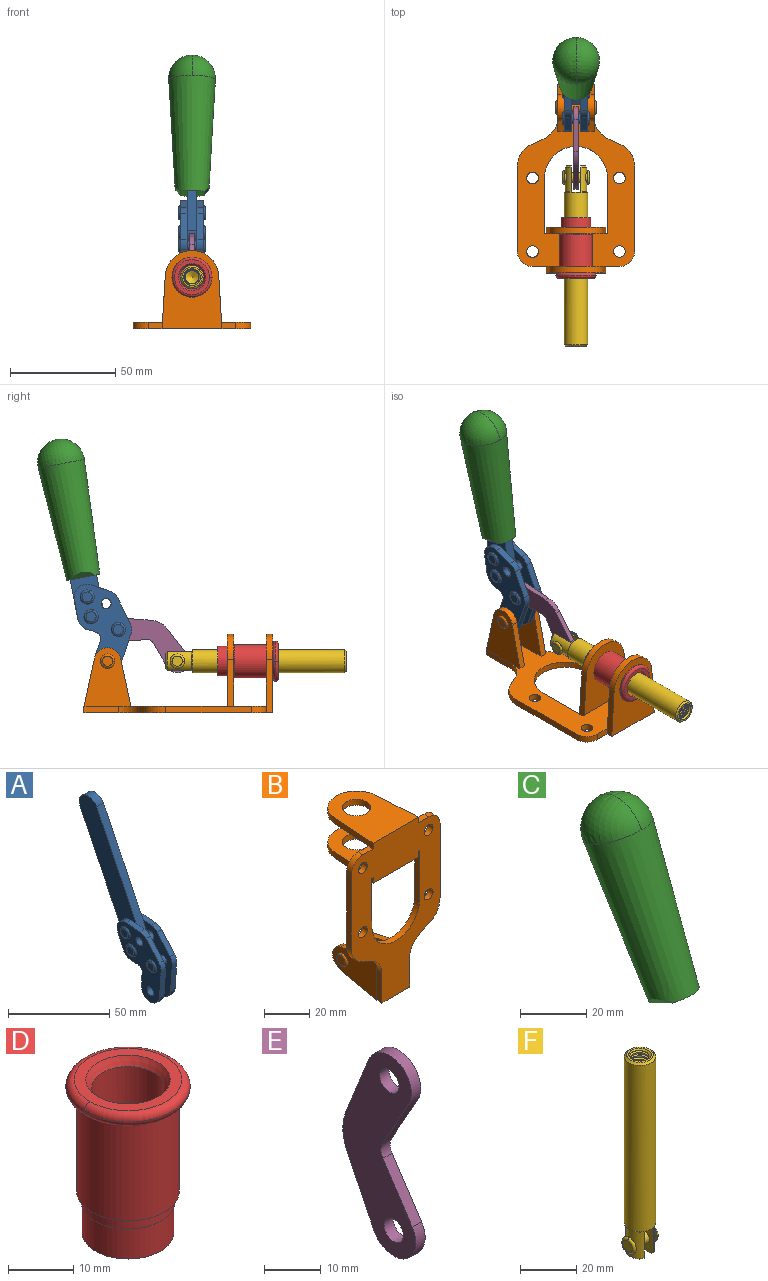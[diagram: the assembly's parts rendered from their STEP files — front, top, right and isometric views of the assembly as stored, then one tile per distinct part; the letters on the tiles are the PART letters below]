
ASSEMBLY  parts=6 mates=6
PART A: 59 faces, bbox 12.9x60.2x99.6 mm
  f0: torus R=2.39mm, axis (-1,0,0), area 14.9mm2, adj f20,f43,f51
  f1: torus R=2.39mm, axis (-1,0,0), area 14.9mm2, adj f19,f42,f51
  f2: torus R=2.39mm, axis (-1,0,0), area 14.9mm2, adj f18,f35,f51
  f3: torus R=2.39mm, axis (-1,0,0), area 14.9mm2, adj f14,f17,f23
  f4: torus R=2.39mm, axis (-1,0,0), area 14.9mm2, adj f13,f16,f23
  f5: torus R=2.39mm, axis (-1,0,0), area 14.9mm2, adj f12,f15,f23
  f6: cylinder r=2.39mm len=4.78mm, axis (1,0,0), area 46.5mm2, adj f48,f50,f51
  f7: cylinder r=2.39mm len=4.78mm, axis (1,0,0), area 46.5mm2, adj f50,f51
  f8: cylinder r=6.35mm len=12.68mm, axis (1,0,0), area 61.8mm2, adj f38,f39,f50,f51
  f9: cylinder r=2.39mm len=4.78mm, axis (-1,0,0), area 70.5mm2, adj f46,f50
  f10: cylinder r=2.39mm len=4.78mm, axis (-1,0,0), area 46.5mm2, adj f23,f45,f46
  f11: cylinder r=2.39mm len=4.78mm, axis (-1,0,0), area 46.5mm2, adj f23,f46
  f12: plane 4.78x4.78mm, normal (1,0,0), area 17.9mm2, adj f5,f15
  f13: plane 4.78x4.78mm, normal (1,0,0), area 17.9mm2, adj f4,f16
  f14: plane 4.78x4.78mm, normal (1,0,0), area 17.9mm2, adj f3,f17
  f15: torus R=2.39mm, axis (-1,0,0), area 14.9mm2, adj f5,f12,f23
  f16: torus R=2.39mm, axis (-1,0,0), area 14.9mm2, adj f4,f13,f23
  f17: torus R=2.39mm, axis (-1,0,0), area 14.9mm2, adj f3,f14,f23
  f18: plane 4.78x4.78mm, normal (-1,0,0), area 17.9mm2, adj f2,f35
  f19: plane 4.78x4.78mm, normal (-1,0,0), area 17.9mm2, adj f1,f42
  f20: plane 4.78x4.78mm, normal (-1,0,0), area 17.9mm2, adj f0,f43
  f21: plane 2.26x0.2mm, normal (1,0,0), area 0.2mm2, adj f31,f44
  f22: plane 2.26x0.2mm, normal (-1,0,0), area 0.2mm2, adj f41,f44
  f23: plane 39.37x30.77mm, normal (1,0,0), area 565.5mm2, adj f3,f4,f5,f10,f11,f15,f16,f17
  f24: cylinder r=6.1mm len=4.15mm, axis (-1,0,0), area 14.7mm2, adj f23,f25,f32,f46
  f25: plane 10.25x9.01mm, normal (0,-0.75,0.66), area 42.3mm2, adj f23,f24,f26,f46
  f26: cylinder r=6.35mm len=4.64mm, axis (-1,0,0), area 15.6mm2, adj f23,f25,f27,f46
  f27: plane 15.84x3.1mm, normal (0,-1,-0.07), area 49.2mm2, adj f23,f26,f28,f46
  f28: cylinder r=6.35mm len=12.68mm, axis (-1,0,0), area 61.8mm2, adj f23,f27,f29,f46
  f29: plane 8.11x3.1mm, normal (0,1,0.07), area 25.2mm2, adj f23,f28,f30,f46
  f30: cylinder r=3.05mm len=3.25mm, axis (-1,0,0), area 14.8mm2, adj f23,f29,f31,f46
  f31: plane 5.99x3.1mm, normal (0,0.07,-1), area 18.6mm2, adj f21,f23,f30,f44,f46
  f32: plane 9.5x3.1mm, normal (0,-0.07,1), area 29.5mm2, adj f23,f24,f33,f46,f47
  f33: cylinder r=6.1mm len=8.63mm, axis (-1,0,0), area 39.1mm2, adj f23,f32,f34,f47
  f34: plane 8.65x3.96mm, normal (0,0.91,-0.42), area 29.5mm2, adj f23,f33,f44,f47
  f35: torus R=2.39mm, axis (-1,0,0), area 14.9mm2, adj f2,f18,f51
  f36: plane 10.25x9.01mm, normal (0,-0.75,0.66), area 42.3mm2, adj f37,f49,f50,f51
  f37: cylinder r=6.35mm len=4.64mm, axis (1,0,0), area 15.6mm2, adj f36,f38,f50,f51
  f38: plane 15.84x3.1mm, normal (0,-1,-0.07), area 49.2mm2, adj f8,f37,f50,f51
  f39: plane 8.11x3.1mm, normal (0,1,0.07), area 25.2mm2, adj f8,f40,f50,f51
  f40: cylinder r=3.05mm len=3.25mm, axis (1,0,0), area 14.8mm2, adj f39,f41,f50,f51
  f41: plane 5.99x3.1mm, normal (0,0.07,-1), area 18.6mm2, adj f22,f40,f44,f50,f51
  f42: torus R=2.39mm, axis (-1,0,0), area 14.9mm2, adj f1,f19,f51
  f43: torus R=2.39mm, axis (-1,0,0), area 14.9mm2, adj f0,f20,f51
  f44: cylinder r=6.35mm len=12.12mm, axis (-1,0,0), area 128.9mm2, adj f21,f22,f23,f31,f34,f41,f46,f47
  f45: plane 2.65x1.35mm, normal (1,0,0), area 1mm2, adj f10,f55
  f46: plane 39.08x20.42mm, normal (-1,0,0), area 412.5mm2, adj f9,f10,f11,f24,f25,f26,f27,f28
  f47: plane 77.62x39.82mm, normal (1,0,0), area 850mm2, adj f32,f33,f34,f44,f53,f54,f55
  f48: plane 2.65x1.35mm, normal (-1,0,0), area 1mm2, adj f6,f55
  f49: cylinder r=6.1mm len=4.15mm, axis (1,0,0), area 14.7mm2, adj f36,f50,f51,f56
  f50: plane 39.08x20.42mm, normal (1,0,0), area 412.5mm2, adj f6,f7,f8,f9,f36,f37,f38,f39
  f51: plane 39.37x30.77mm, normal (-1,0,0), area 565.5mm2, adj f0,f1,f2,f6,f7,f8,f35,f36
  f52: plane 8.65x3.96mm, normal (0,0.91,-0.42), area 29.5mm2, adj f44,f51,f57,f58
  f53: plane 68.49x33.4mm, normal (0,0.9,-0.44), area 358.1mm2, adj f44,f47,f54,f58
  f54: cylinder r=6.35mm len=12.06mm, axis (1,0,0), area 93.7mm2, adj f47,f53,f55,f58
  f55: plane 68.49x33.4mm, normal (0,-0.9,0.44), area 358.1mm2, adj f44,f45,f46,f47,f48,f50,f54,f58
  f56: plane 9.5x3.1mm, normal (0,-0.07,1), area 29.5mm2, adj f49,f50,f51,f57,f58
  f57: cylinder r=6.1mm len=8.63mm, axis (1,0,0), area 39.1mm2, adj f51,f52,f56,f58
  f58: plane 77.62x39.82mm, normal (-1,0,0), area 850mm2, adj f44,f52,f53,f54,f55,f56,f57
PART B: 55 faces, bbox 55.7x37.4x89.8 mm
  f0: torus R=2.41mm, axis (-1,0,0), area 15mm2, adj f11,f15,f25
  f1: torus R=2.41mm, axis (-1,0,0), area 15mm2, adj f10,f12,f22
  f2: cylinder r=2.78mm len=5.56mm, axis (0,-1,0), area 54.2mm2, adj f30,f54
  f3: cylinder r=14.99mm len=29.97mm, axis (0,-1,0), area 145.9mm2, adj f30,f49,f53,f54
  f4: cylinder r=2.78mm len=5.56mm, axis (0,-1,0), area 54.2mm2, adj f30,f54
  f5: cylinder r=2.78mm len=5.56mm, axis (0,-1,0), area 54.2mm2, adj f30,f54
  f6: cylinder r=2.78mm len=5.56mm, axis (0,-1,0), area 54.2mm2, adj f30,f54
  f7: cylinder r=6.35mm len=12.7mm, axis (0,0,1), area 123.6mm2, adj f27,f51
  f8: cylinder r=6.35mm len=12.7mm, axis (0,0,-1), area 124.7mm2, adj f21,f35
  f9: cylinder r=2.41mm len=11.18mm, axis (-1,0,0), area 169.4mm2, adj f16,f19
  f10: plane 4.83x4.83mm, normal (1,0,0), area 18.3mm2, adj f1,f12
  f11: plane 4.83x4.83mm, normal (-1,0,0), area 18.3mm2, adj f0,f15
  f12: torus R=2.41mm, axis (-1,0,0), area 15mm2, adj f1,f10,f22
  f13: cylinder r=6.35mm len=12.41mm, axis (1,0,0), area 53.4mm2, adj f18,f19,f22,f23
  f14: cylinder r=6.35mm len=12.41mm, axis (-1,0,0), area 53.4mm2, adj f16,f17,f24,f25
  f15: torus R=2.41mm, axis (-1,0,0), area 15mm2, adj f0,f11,f25
  f16: plane 27.86x22.35mm, normal (1,0,0), area 425.4mm2, adj f9,f14,f17,f24,f30
  f17: plane 22.86x4.97mm, normal (0,0.21,0.98), area 72.5mm2, adj f14,f16,f25,f30
  f18: plane 22.86x4.97mm, normal (0,0.21,0.98), area 72.5mm2, adj f13,f19,f22,f30
  f19: plane 27.86x22.35mm, normal (-1,0,0), area 425.4mm2, adj f9,f13,f18,f23,f30
  f20: cylinder r=12.7mm len=25.35mm, axis (0,0,-1), area 119.8mm2, adj f21,f34,f35,f36
  f21: plane 34.21x28.07mm, normal (0,0,-1), area 702.4mm2, adj f8,f20,f30,f34,f36
  f22: plane 27.96x22.45mm, normal (1,0,0), area 407.2mm2, adj f1,f12,f13,f18,f23,f30,f42,f43
  f23: plane 22.86x4.97mm, normal (0,0.21,-0.98), area 72.5mm2, adj f13,f19,f22,f44
  f24: plane 22.86x4.97mm, normal (0,0.21,-0.98), area 72.5mm2, adj f14,f16,f25,f44
  f25: plane 27.86x22.35mm, normal (-1,0,0), area 407.1mm2, adj f0,f14,f15,f17,f24,f30,f45,f46
  f26: plane 3.1x0.95mm, normal (0,0,-1), area 2.7mm2, adj f30,f49,f50,f54
  f27: plane 34.21x28.07mm, normal (0,0,1), area 702.4mm2, adj f7,f28,f30,f50,f52
  f28: cylinder r=12.7mm len=25.35mm, axis (0,0,1), area 118.8mm2, adj f27,f50,f51,f52
  f29: plane 3.1x0.95mm, normal (0,0,-1), area 2.7mm2, adj f30,f52,f53,f54
  f30: plane 86.54x55.63mm, normal (0,1,0), area 2362.9mm2, adj f2,f3,f4,f5,f6,f16,f17,f18
  f31: plane 40.56x3.1mm, normal (-1,0,0), area 125.7mm2, adj f30,f32,f48,f54
  f32: cylinder r=7.11mm len=7.11mm, axis (0,-1,0), area 34.6mm2, adj f30,f31,f33,f54
  f33: plane 6.67x3.1mm, normal (0,0,1), area 20.4mm2, adj f30,f32,f34,f54
  f34: plane 25.39x3.13mm, normal (-1,0.06,0), area 79.5mm2, adj f20,f21,f33,f35,f54
  f35: plane 37.31x28.45mm, normal (0,0,1), area 789.9mm2, adj f8,f20,f34,f36,f54
  f36: plane 25.39x3.13mm, normal (1,0.06,0), area 79.5mm2, adj f20,f21,f35,f37,f54
  f37: plane 6.67x3.1mm, normal (0,0,1), area 20.4mm2, adj f30,f36,f38,f54
  f38: cylinder r=7.11mm len=7.11mm, axis (0,-1,0), area 34.6mm2, adj f30,f37,f39,f54
  f39: plane 40.56x3.1mm, normal (1,0,0), area 125.7mm2, adj f30,f38,f40,f54
  f40: cylinder r=11.18mm len=10.16mm, axis (0,-1,0), area 39.5mm2, adj f30,f39,f41,f54
  f41: plane 6.09x3.1mm, normal (0.42,0,-0.91), area 20.8mm2, adj f30,f40,f42,f54
  f42: cylinder r=11.18mm len=9.41mm, axis (0,-1,0), area 37.2mm2, adj f22,f30,f41,f43,f54
  f43: plane 16.5x3.1mm, normal (1,0,0), area 51.1mm2, adj f22,f42,f44,f54
  f44: plane 17.37x3.1mm, normal (0,0,-1), area 53.8mm2, adj f23,f24,f30,f43,f45,f54
  f45: plane 16.5x3.1mm, normal (-1,0,0), area 51.1mm2, adj f25,f44,f46,f54
  f46: cylinder r=11.18mm len=9.41mm, axis (0,-1,0), area 37.2mm2, adj f25,f30,f45,f47,f54
  f47: plane 6.09x3.1mm, normal (-0.42,0,-0.91), area 20.8mm2, adj f30,f46,f48,f54
  f48: cylinder r=11.18mm len=10.16mm, axis (0,-1,0), area 39.5mm2, adj f30,f31,f47,f54
  f49: plane 26.54x3.1mm, normal (-1,0,0), area 82.3mm2, adj f3,f26,f30,f54
  f50: plane 25.39x3.1mm, normal (1,0.06,0), area 78.8mm2, adj f26,f27,f28,f51,f54
  f51: plane 37.31x28.45mm, normal (0,0,-1), area 789.9mm2, adj f7,f28,f50,f52,f54
  f52: plane 25.39x3.1mm, normal (-1,0.06,0), area 78.8mm2, adj f27,f28,f29,f51,f54
  f53: plane 26.54x3.1mm, normal (1,0,0), area 82.3mm2, adj f3,f29,f30,f54
  f54: plane 89.66x55.63mm, normal (0,-1,0), area 2678.5mm2, adj f2,f3,f4,f5,f6,f26,f29,f31
PART C: 11 faces, bbox 22.3x42.6x64.5 mm
  f0: sphere r=11.13mm, area 411.4mm2, adj f1,f8
  f1: cone r=11.11mm half-angle=3.3deg, axis (0,0.44,0.9), area 3251.8mm2, adj f0,f7,f8,f9,f10
  f2: cylinder r=6.16mm len=11.7mm, axis (1,0,0), area 89.5mm2, adj f3,f4,f5,f6
  f3: plane 60.23x36.75mm, normal (-1,0,0), area 763.6mm2, adj f2,f4,f6,f10
  f4: plane 51.37x25.05mm, normal (0,0.9,-0.44), area 264.2mm2, adj f2,f3,f5,f10
  f5: plane 60.23x36.75mm, normal (1,0,0), area 763.6mm2, adj f2,f4,f6,f10
  f6: plane 51.37x25.05mm, normal (0,-0.9,0.44), area 264.2mm2, adj f2,f3,f5,f10
  f7: plane 9.95x5.95mm, normal (0.71,-0.31,-0.64), area 25.8mm2, adj f1,f10
  f8: sphere r=11.13mm, area 411.4mm2, adj f0,f1
  f9: plane 9.95x5.95mm, normal (-0.71,-0.31,-0.64), area 25.8mm2, adj f1,f10
  f10: plane 14.27x11.38mm, normal (0,-0.44,-0.9), area 106.7mm2, adj f1,f3,f4,f5,f6,f7,f9
PART D: 15 faces, bbox 20.6x20.6x28.7 mm
  f0: torus R=8.26mm, axis (0,0,1), area 56.8mm2, adj f1,f10,f12
  f1: torus R=8.26mm, axis (0,0,1), area 56.8mm2, adj f0,f6,f13
  f2: cylinder r=5.59mm len=25.91mm, axis (0,0,1), area 909.6mm2, adj f3,f4
  f3: cone r=6.86mm half-angle=45deg, axis (0,0,-1), area 70.2mm2, adj f2,f14
  f4: cone r=6.47mm half-angle=30deg, axis (0,0,1), area 66.7mm2, adj f2,f13
  f5: cylinder r=7.04mm len=14.07mm, axis (0,0,1), area 252.6mm2, adj f11,f14
  f6: torus R=8.26mm, axis (0,0,1), area 56.8mm2, adj f1,f12,f13
  f7: cylinder r=7.16mm len=14.33mm, axis (0,0,1), area 91.5mm2, adj f9,f11
  f8: cylinder r=7.86mm len=18.42mm, axis (0,0,1), area 909.6mm2, adj f9,f10
  f9: plane 15.72x15.72mm, normal (0,0,-1), area 33mm2, adj f7,f8
  f10: plane 16.51x16.51mm, normal (0,0,-1), area 19.9mm2, adj f0,f8,f12
  f11: plane 14.33x14.33mm, normal (0,0,-1), area 5.7mm2, adj f5,f7
  f12: torus R=8.26mm, axis (0,0,1), area 56.8mm2, adj f0,f6,f10
  f13: plane 16.51x16.51mm, normal (0,0,1), area 82.7mm2, adj f1,f4,f6
  f14: plane 14.07x14.07mm, normal (0,0,-1), area 7.8mm2, adj f3,f5
PART E: 12 faces, bbox 2.3x18.2x42.8 mm
  f0: cylinder r=2.4mm len=4.8mm, axis (1,0,0), area 34.9mm2, adj f4,f11
  f1: cylinder r=10.41mm len=8.47mm, axis (1,0,0), area 20.2mm2, adj f4,f9,f10,f11
  f2: cylinder r=3.05mm len=3.16mm, axis (1,0,0), area 7.7mm2, adj f4,f6,f7,f11
  f3: cylinder r=2.4mm len=4.8mm, axis (1,0,0), area 34.9mm2, adj f4,f11
  f4: plane 42.81x18.23mm, normal (-1,0,0), area 414.1mm2, adj f0,f1,f2,f3,f5,f6,f7,f8
  f5: cylinder r=5.54mm len=10.67mm, axis (1,0,0), area 41.8mm2, adj f4,f6,f10,f11
  f6: plane 11.66x6.53mm, normal (0,-0.87,-0.49), area 30.9mm2, adj f2,f4,f5,f11
  f7: plane 11.17x7.33mm, normal (0,-0.84,0.55), area 30.9mm2, adj f2,f4,f8,f11
  f8: cylinder r=5.54mm len=10.51mm, axis (1,0,0), area 41.8mm2, adj f4,f7,f9,f11
  f9: plane 13.67x6.67mm, normal (0,0.9,-0.44), area 35.1mm2, adj f1,f4,f8,f11
  f10: plane 14.1x5.7mm, normal (0,0.93,0.37), area 35.1mm2, adj f1,f4,f5,f11
  f11: plane 42.81x18.23mm, normal (1,0,0), area 414.1mm2, adj f0,f1,f2,f3,f5,f6,f7,f8
PART F: 48 faces, bbox 12.6x11.1x86.1 mm
  f0: torus R=2.41mm, axis (-1,0,0), area 15mm2, adj f30,f32,f34
  f1: torus R=2.41mm, axis (-1,0,0), area 15mm2, adj f29,f31,f33
  f2: cylinder r=5.54mm len=72.39mm, axis (0,0,1), area 2518.5mm2, adj f3,f4,f42,f43
  f3: cone r=5.54mm half-angle=45deg, axis (0,0,1), area 7.6mm2, adj f2,f5,f41
  f4: cone r=5.54mm half-angle=45deg, axis (0,0,-1), area 34.9mm2, adj f2,f39
  f5: cylinder r=5.08mm len=11.48mm, axis (0,0,1), area 108.3mm2, adj f3,f7,f8,f41
  f6: cylinder r=2.41mm len=4.83mm, axis (-1,0,0), area 71.2mm2, adj f40,f41
  f7: cylinder r=2.41mm len=4.83mm, axis (-1,0,0), area 7.6mm2, adj f5,f34
  f8: cone r=5.08mm half-angle=45deg, axis (0,0,1), area 10.6mm2, adj f5,f37,f41
  f9: cone r=3.98mm half-angle=45deg, axis (0,0,1), area 17.6mm2, adj f27,f39,f45,f46,f47
  f10: cylinder r=2.41mm len=4.83mm, axis (-1,0,0), area 7.6mm2, adj f33,f38
  f11: cylinder r=3.2mm len=6.4mm, axis (0,0,1), area 78.4mm2, adj f12,f28,f44,f45,f47
  f12: cylinder r=3.2mm len=6.4mm, axis (0,0,1), area 10.5mm2, adj f11,f13,f45,f47
  f13: cylinder r=3.2mm len=6.4mm, axis (0,0,1), area 10.5mm2, adj f12,f14,f45,f47
  f14: cylinder r=3.2mm len=6.4mm, axis (0,0,1), area 10.5mm2, adj f13,f15,f45,f47
  f15: cylinder r=3.2mm len=6.4mm, axis (0,0,1), area 10.5mm2, adj f14,f16,f45,f47
  f16: cylinder r=3.2mm len=6.4mm, axis (0,0,1), area 10.5mm2, adj f15,f17,f45,f47
  f17: cylinder r=3.2mm len=6.4mm, axis (0,0,1), area 10.5mm2, adj f16,f18,f45,f47
  f18: cylinder r=3.2mm len=6.4mm, axis (0,0,1), area 10.5mm2, adj f17,f19,f45,f47
  f19: cylinder r=3.2mm len=6.4mm, axis (0,0,1), area 10.5mm2, adj f18,f20,f45,f47
  f20: cylinder r=3.2mm len=6.4mm, axis (0,0,1), area 10.5mm2, adj f19,f21,f45,f47
  f21: cylinder r=3.2mm len=6.4mm, axis (0,0,1), area 10.5mm2, adj f20,f22,f45,f47
  f22: cylinder r=3.2mm len=6.4mm, axis (0,0,1), area 10.5mm2, adj f21,f23,f45,f47
  f23: cylinder r=3.2mm len=6.4mm, axis (0,0,1), area 10.5mm2, adj f22,f24,f45,f47
  f24: cylinder r=3.2mm len=6.4mm, axis (0,0,1), area 10.5mm2, adj f23,f25,f45,f47
  f25: cylinder r=3.2mm len=6.4mm, axis (0,0,1), area 10.5mm2, adj f24,f26,f45,f47
  f26: cylinder r=3.2mm len=6.4mm, axis (0,0,1), area 10.5mm2, adj f25,f27,f45,f47
  f27: cylinder r=3.2mm len=6.4mm, axis (0,0,1), area 7.4mm2, adj f9,f26,f45,f47
  f28: cone r=3.2mm half-angle=60deg, axis (0,0,1), area 37.2mm2, adj f11
  f29: plane 4.83x4.83mm, normal (-1,0,0), area 18.3mm2, adj f1,f31
  f30: plane 4.83x4.83mm, normal (1,0,0), area 18.3mm2, adj f0,f32
  f31: torus R=2.41mm, axis (-1,0,0), area 15mm2, adj f1,f29,f33
  f32: torus R=2.41mm, axis (-1,0,0), area 15mm2, adj f0,f30,f34
  f33: plane 6.83x6.83mm, normal (1,0,0), area 18.3mm2, adj f1,f10,f31
  f34: plane 6.83x6.83mm, normal (-1,0,0), area 18.3mm2, adj f0,f7,f32
  f35: cone r=5.08mm half-angle=45deg, axis (0,0,1), area 10.6mm2, adj f36,f38,f40
  f36: plane 7.25x1.97mm, normal (0,0,-1), area 10mm2, adj f35,f40
  f37: plane 7.25x1.97mm, normal (0,0,-1), area 10mm2, adj f8,f41
  f38: cylinder r=5.08mm len=11.48mm, axis (0,0,1), area 108.3mm2, adj f10,f35,f40,f42
  f39: plane 9.55x9.55mm, normal (0,0,1), area 22mm2, adj f4,f9
  f40: plane 12.76x10.09mm, normal (1,0,0), area 95.7mm2, adj f6,f35,f36,f38,f42,f43
  f41: plane 12.76x10.09mm, normal (-1,0,0), area 95.7mm2, adj f3,f5,f6,f8,f37,f43
  f42: cone r=5.54mm half-angle=45deg, axis (0,0,1), area 7.6mm2, adj f2,f38,f40
  f43: plane 11.07x4.7mm, normal (0,0,-1), area 50.4mm2, adj f2,f40,f41
  f44: plane 0.89x0.62mm, normal (-1,0,0), area 0.3mm2, adj f11,f45,f46,f47
  f45: bspline ~24.8x7.63mm, area 266.6mm2, adj f9,f11,f12,f13,f14,f15,f16,f17
  f46: bspline ~24.87x7.63mm, area 73.6mm2, adj f9,f44,f45,f47
  f47: bspline ~24.98x7.63mm, area 272.5mm2, adj f9,f11,f12,f13,f14,f15,f16,f17
PLACE A rot(axis=(1,0,0),15deg) t=(0,9.15,49.24)mm
PLACE B rot(axis=(1,0,0),90deg) t=(0,9.14,0)mm fixed
PLACE C rot(axis=(1,0,0),15deg) t=(0.04,9.15,49.24)mm
PLACE D rot(axis=(1,0,0),90deg) t=(0,9.14,0)mm
PLACE E rot(axis=(0,-0.53,-0.85),180deg) t=(0,33.05,10.71)mm
PLACE F rot(axis=(1,0,0),90deg) t=(0,23.56,0)mm
MATE fastened D.f2 <-> B.f7  axis (0,-1,0) through (0,-37.25,24.61)mm
MATE revolute A.f7 <-> B.f0  axis (-1,0,0) through (0,41.23,24.61)mm
MATE fastened C.f2 <-> A.f54  axis (-1,0,0) through (2.35,63.6,120.54)mm
MATE slider F.f2 <-> D.f2  axis (0,-1,0) through (0,-35.22,24.61)mm
MATE revolute E.f3 <-> F.f6  axis (-1,0,0) through (0,8.09,24.61)mm
MATE revolute E.f5 <-> A.f4  axis (-1,0,0) through (0,36.06,39.62)mm
